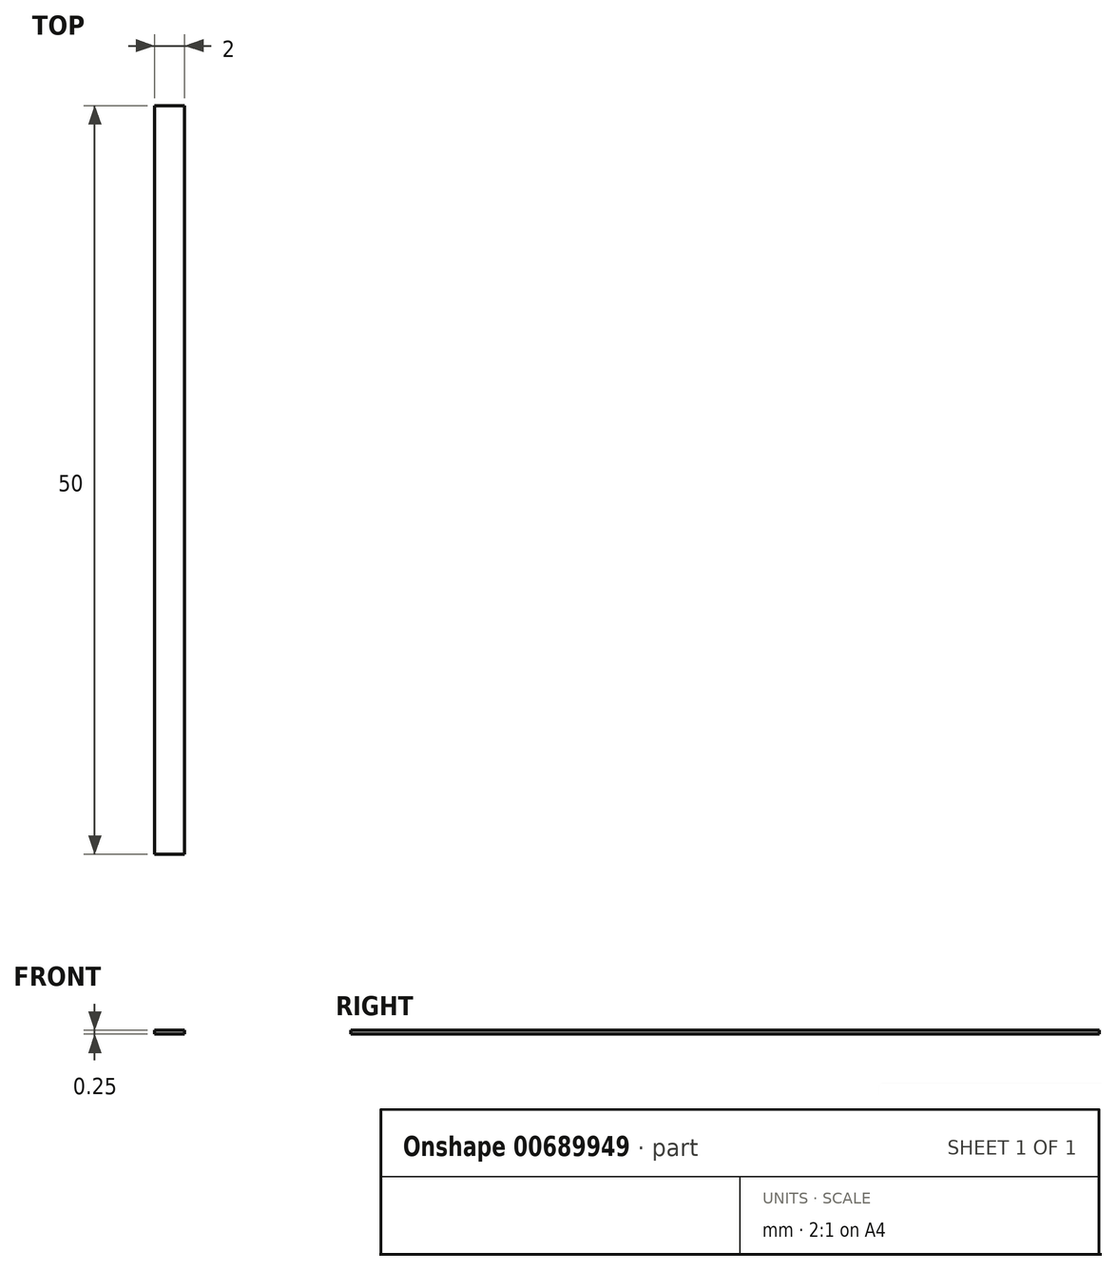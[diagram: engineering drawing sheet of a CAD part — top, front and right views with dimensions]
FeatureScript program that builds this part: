
annotation { "Feature Type Name" : "Feature", "Feature Type Description" : "" }
export const myFeature = defineFeature(function(context is Context, id is Id, definition is map)
    precondition{}
    {
        {
            var Q0;
            Q0=qCreatedBy(makeId("Top.planeOp"),FACE);
            var sketch = newSketch(context, id + "F0", { "sketchPlane" : qUnion([Q0])});
            skLineSegment(sketch, "E0.bottom", {"start": v(0, 0) * mm, "end": v(2, 0) * mm});
            skLineSegment(sketch, "E0.top", {"start": v(0, 50) * mm, "end": v(2, 50) * mm});
            skLineSegment(sketch, "E0.left", {"start": v(0, 0) * mm, "end": v(0, 50) * mm});
            skLineSegment(sketch, "E0.right", {"start": v(2, 0) * mm, "end": v(2, 50) * mm});
            skSolve(sketch);
        }
        {
            var Q0;
            Q0 = qSketchRegion(id + "F0", true);
            extrude(context, id + "F1", {"entities" : qUnion([Q0]), "depth" : .25 * mm, "offsetDistance" : 25 * mm});
        }
    });
